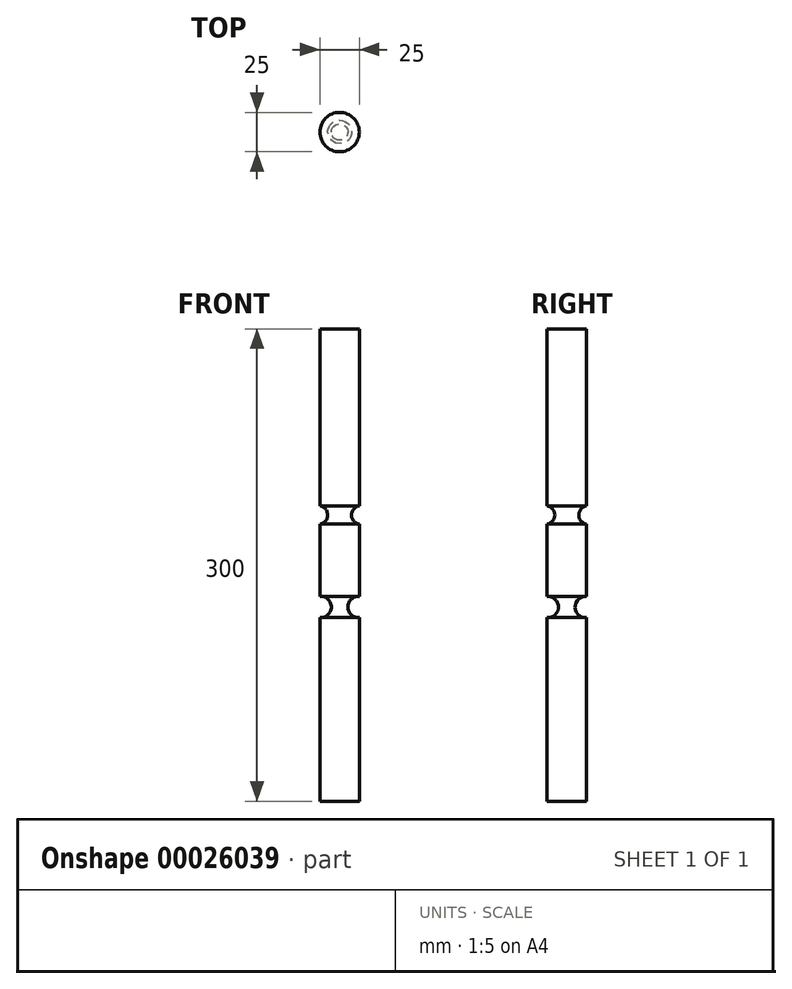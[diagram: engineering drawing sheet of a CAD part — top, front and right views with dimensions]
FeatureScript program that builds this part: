
annotation { "Feature Type Name" : "Feature", "Feature Type Description" : "" }
export const myFeature = defineFeature(function(context is Context, id is Id, definition is map)
    precondition{}
    {
        {
            var Q0;
            Q0=qCreatedBy(makeId("Top.planeOp"),FACE);
            var sketch = newSketch(context, id + "F0", { "sketchPlane" : qUnion([Q0])});
            skCircle(sketch, "E0", {"center": v(0, 0) * mm, "radius": 12.5 * mm});
            skSolve(sketch);
        }
        {
            var Q0;
            Q0 = qSketchRegion(id + "F0", true);
            extrude(context, id + "F1", {"entities" : qUnion([Q0]), "depth" : 300 * mm});
        }
        {
            var Q0;
            Q0=qCreatedBy(makeId("Right.planeOp"),FACE);
            var sketch = newSketch(context, id + "F2", { "sketchPlane" : qUnion([Q0])});
            skCircle(sketch, "E1", {"center": v(-11.98, 123.33) * mm, "radius": 6.73 * mm});
            skCircle(sketch, "E2", {"center": v(-13.47, 181.74) * mm, "radius": 5.9 * mm});
            skSolve(sketch);
        }
        {
            var Q0;
            Q0 = qSketchRegion(id + "F2", true);
            var Q1;
            Q1=makeQuery(id+"F1.opExtrude","CAP_EDGE",EDGE,{"disambiguationData":[OSD([sQuery(id+"F0.wireOp",EDGE,"E0")])],"isStart":false});
            revolve(context, id + "F3", {"operationType" : NewBodyOperationType.REMOVE, "entities" : qUnion([Q0]), "axis" : qUnion([Q1]), "revolveType" : RevolveType.FULL});
        }
    });
